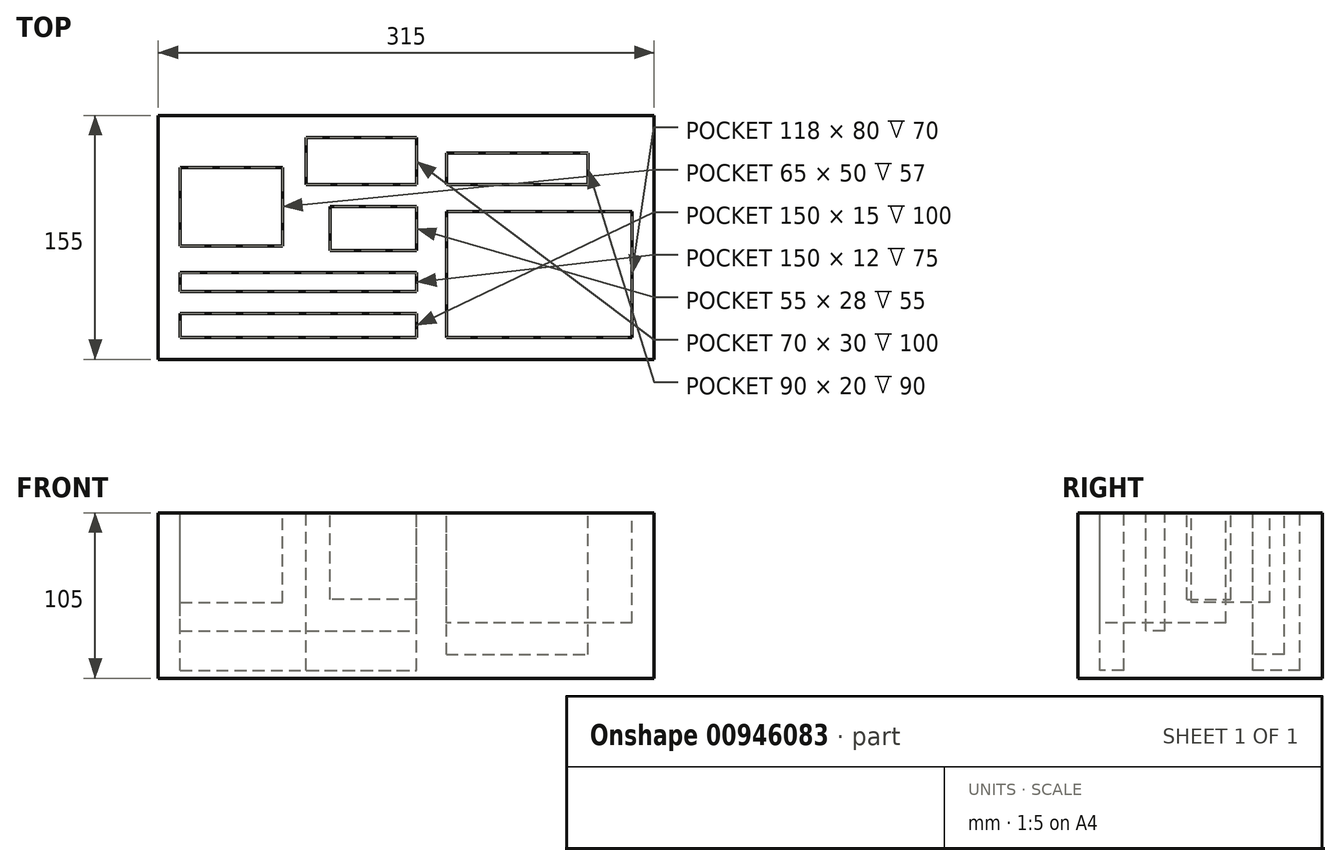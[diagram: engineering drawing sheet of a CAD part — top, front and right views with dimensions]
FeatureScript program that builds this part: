
annotation { "Feature Type Name" : "Feature", "Feature Type Description" : "" }
export const myFeature = defineFeature(function(context is Context, id is Id, definition is map)
    precondition{}
    {
        {
            var Q0;
            Q0=qCreatedBy(makeId("Top.planeOp"),FACE);
            var sketch = newSketch(context, id + "F0", { "sketchPlane" : qUnion([Q0])});
            skLineSegment(sketch, "E0.bottom", {"start": v(-283.8, 138.94) * mm, "end": v(31.2, 138.94) * mm});
            skLineSegment(sketch, "E0.top", {"start": v(-283.8, -16.06) * mm, "end": v(31.2, -16.06) * mm});
            skLineSegment(sketch, "E0.left", {"start": v(-283.8, 138.94) * mm, "end": v(-283.8, -16.06) * mm});
            skLineSegment(sketch, "E0.right", {"start": v(31.2, 138.94) * mm, "end": v(31.2, -16.06) * mm});
            skSolve(sketch);
        }
        {
            var Q0;
            Q0 = qSketchRegion(id + "F0", true);
            extrude(context, id + "F1", {"entities" : qUnion([Q0]), "depth" : 105 * mm, "offsetDistance" : 25 * mm});
        }
        {
            var Q0;
            Q0=makeQuery(id+"F1.opExtrude","CAP_FACE",FACE,{"disambiguationData":[OSD([sQuery(id+"F0.wireOp",EDGE,"E0.bottom"),sQuery(id+"F0.wireOp",EDGE,"E0.top"),sQuery(id+"F0.wireOp",EDGE,"E0.left"),sQuery(id+"F0.wireOp",EDGE,"E0.right")])],"isStart":false});
            var sketch = newSketch(context, id + "F2", { "sketchPlane" : qUnion([Q0])});
            skLineSegment(sketch, "E1.bottom", {"start": v(17.2, 77.94) * mm, "end": v(-100.8, 77.94) * mm});
            skLineSegment(sketch, "E1.top", {"start": v(17.2, -2.06) * mm, "end": v(-100.8, -2.06) * mm});
            skLineSegment(sketch, "E1.left", {"start": v(17.2, 77.94) * mm, "end": v(17.2, -2.06) * mm});
            skLineSegment(sketch, "E1.right", {"start": v(-100.8, 77.94) * mm, "end": v(-100.8, -2.06) * mm});
            skSolve(sketch);
        }
        {
            var Q0;
            Q0 = qSketchRegion(id + "F2", true);
            extrude(context, id + "F3", {"entities" : qUnion([Q0]), "operationType" : NewBodyOperationType.REMOVE, "oppositeDirection" : true, "depth" : 70 * mm, "offsetDistance" : 25 * mm});
        }
        {
            var Q0;
            Q0=makeQuery(id+"F1.opExtrude","CAP_FACE",FACE,{"disambiguationData":[OSD([sQuery(id+"F0.wireOp",EDGE,"E0.bottom"),sQuery(id+"F0.wireOp",EDGE,"E0.top"),sQuery(id+"F0.wireOp",EDGE,"E0.left"),sQuery(id+"F0.wireOp",EDGE,"E0.right")])],"isStart":false});
            var sketch = newSketch(context, id + "F4", { "sketchPlane" : qUnion([Q0])});
            skLineSegment(sketch, "E2.bottom", {"start": v(-269.8, 105.88) * mm, "end": v(-204.8, 105.88) * mm});
            skLineSegment(sketch, "E2.top", {"start": v(-269.8, 55.88) * mm, "end": v(-204.8, 55.88) * mm});
            skLineSegment(sketch, "E2.left", {"start": v(-269.8, 105.88) * mm, "end": v(-269.8, 55.88) * mm});
            skLineSegment(sketch, "E2.right", {"start": v(-204.8, 105.88) * mm, "end": v(-204.8, 55.88) * mm});
            skSolve(sketch);
        }
        {
            var Q0;
            Q0 = qSketchRegion(id + "F4", true);
            extrude(context, id + "F5", {"entities" : qUnion([Q0]), "operationType" : NewBodyOperationType.REMOVE, "oppositeDirection" : true, "depth" : 57 * mm, "offsetDistance" : 25 * mm});
        }
        {
            var Q0;
            Q0=makeQuery(id+"F4.imprint","IMPRINT",FACE,{"disambiguationData":[TD([[makeQuery(id+"F4.imprint","IMPRINT",EDGE,{"derivedFrom":sQuery(id+"F4.wireOp",EDGE,"E2.bottom")}),1.0]])]});
            var sketch = newSketch(context, id + "F6", { "sketchPlane" : qUnion([Q0])});
            skLineSegment(sketch, "E3.bottom", {"start": v(-269.8, 12.94) * mm, "end": v(-119.8, 12.94) * mm});
            skLineSegment(sketch, "E3.top", {"start": v(-269.8, -2.06) * mm, "end": v(-119.8, -2.06) * mm});
            skLineSegment(sketch, "E3.left", {"start": v(-269.8, 12.94) * mm, "end": v(-269.8, -2.06) * mm});
            skLineSegment(sketch, "E3.right", {"start": v(-119.8, 12.94) * mm, "end": v(-119.8, -2.06) * mm});
            skSolve(sketch);
        }
        {
            var Q0;
            Q0 = qSketchRegion(id + "F6", true);
            extrude(context, id + "F7", {"entities" : qUnion([Q0]), "operationType" : NewBodyOperationType.REMOVE, "oppositeDirection" : true, "depth" : 100 * mm, "offsetDistance" : 25 * mm});
        }
        {
            var Q0;
            Q0=makeQuery(id+"F4.imprint","IMPRINT",FACE,{"disambiguationData":[TD([[makeQuery(id+"F4.imprint","IMPRINT",EDGE,{"derivedFrom":sQuery(id+"F4.wireOp",EDGE,"E2.bottom")}),1.0]])]});
            var sketch = newSketch(context, id + "F8", { "sketchPlane" : qUnion([Q0])});
            skLineSegment(sketch, "E4.bottom", {"start": v(-269.8, 38.94) * mm, "end": v(-119.8, 38.94) * mm});
            skLineSegment(sketch, "E4.top", {"start": v(-269.8, 26.94) * mm, "end": v(-119.8, 26.94) * mm});
            skLineSegment(sketch, "E4.left", {"start": v(-269.8, 38.94) * mm, "end": v(-269.8, 26.94) * mm});
            skLineSegment(sketch, "E4.right", {"start": v(-119.8, 38.94) * mm, "end": v(-119.8, 26.94) * mm});
            skSolve(sketch);
        }
        {
            var Q0;
            Q0 = qSketchRegion(id + "F8", true);
            extrude(context, id + "F9", {"entities" : qUnion([Q0]), "operationType" : NewBodyOperationType.REMOVE, "oppositeDirection" : true, "depth" : 75 * mm, "offsetDistance" : 25 * mm});
        }
        {
            var Q0;
            Q0=makeQuery(id+"F4.imprint","IMPRINT",FACE,{"disambiguationData":[TD([[makeQuery(id+"F4.imprint","IMPRINT",EDGE,{"derivedFrom":sQuery(id+"F4.wireOp",EDGE,"E2.bottom")}),1.0]])]});
            var sketch = newSketch(context, id + "F10", { "sketchPlane" : qUnion([Q0])});
            skLineSegment(sketch, "E5.bottom", {"start": v(-119.8, 52.94) * mm, "end": v(-174.8, 52.94) * mm});
            skLineSegment(sketch, "E5.top", {"start": v(-119.8, 80.94) * mm, "end": v(-174.8, 80.94) * mm});
            skLineSegment(sketch, "E5.left", {"start": v(-119.8, 52.94) * mm, "end": v(-119.8, 80.94) * mm});
            skLineSegment(sketch, "E5.right", {"start": v(-174.8, 52.94) * mm, "end": v(-174.8, 80.94) * mm});
            skSolve(sketch);
        }
        {
            var Q0;
            Q0=makeQuery(id+"F10.imprint","IMPRINT",FACE,{"disambiguationData":[TD([[makeQuery(id+"F10.imprint","IMPRINT",EDGE,{"derivedFrom":sQuery(id+"F10.wireOp",EDGE,"E5.bottom")}),-1.0]])]});
            extrude(context, id + "F11", {"entities" : qUnion([Q0]), "operationType" : NewBodyOperationType.REMOVE, "oppositeDirection" : true, "depth" : 55 * mm, "offsetDistance" : 25 * mm});
        }
        {
            var Q0;
            Q0=makeQuery(id+"F4.imprint","IMPRINT",FACE,{"disambiguationData":[TD([[makeQuery(id+"F4.imprint","IMPRINT",EDGE,{"derivedFrom":sQuery(id+"F4.wireOp",EDGE,"E2.bottom")}),1.0]])]});
            var sketch = newSketch(context, id + "F12", { "sketchPlane" : qUnion([Q0])});
            skLineSegment(sketch, "E6.bottom", {"start": v(-189.8, 124.94) * mm, "end": v(-119.8, 124.94) * mm});
            skLineSegment(sketch, "E6.top", {"start": v(-189.8, 94.94) * mm, "end": v(-119.8, 94.94) * mm});
            skLineSegment(sketch, "E6.left", {"start": v(-189.8, 124.94) * mm, "end": v(-189.8, 94.94) * mm});
            skLineSegment(sketch, "E6.right", {"start": v(-119.8, 124.94) * mm, "end": v(-119.8, 94.94) * mm});
            skSolve(sketch);
        }
        {
            var Q0;
            Q0 = qSketchRegion(id + "F12", true);
            extrude(context, id + "F13", {"entities" : qUnion([Q0]), "operationType" : NewBodyOperationType.REMOVE, "oppositeDirection" : true, "depth" : 100 * mm, "offsetDistance" : 25 * mm});
        }
        {
            var Q0;
            Q0=makeQuery(id+"F4.imprint","IMPRINT",FACE,{"disambiguationData":[TD([[makeQuery(id+"F4.imprint","IMPRINT",EDGE,{"derivedFrom":sQuery(id+"F4.wireOp",EDGE,"E2.bottom")}),1.0]])]});
            var sketch = newSketch(context, id + "F14", { "sketchPlane" : qUnion([Q0])});
            skLineSegment(sketch, "E7.bottom", {"start": v(-100.8, 114.94) * mm, "end": v(-10.8, 114.94) * mm});
            skLineSegment(sketch, "E7.top", {"start": v(-100.8, 94.94) * mm, "end": v(-10.8, 94.94) * mm});
            skLineSegment(sketch, "E7.left", {"start": v(-100.8, 114.94) * mm, "end": v(-100.8, 94.94) * mm});
            skLineSegment(sketch, "E7.right", {"start": v(-10.8, 114.94) * mm, "end": v(-10.8, 94.94) * mm});
            skSolve(sketch);
        }
        {
            var Q0;
            Q0 = qSketchRegion(id + "F14", true);
            extrude(context, id + "F15", {"entities" : qUnion([Q0]), "operationType" : NewBodyOperationType.REMOVE, "oppositeDirection" : true, "depth" : 90 * mm, "offsetDistance" : 25 * mm});
        }
    });
